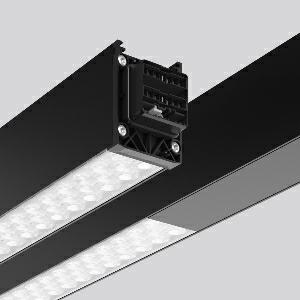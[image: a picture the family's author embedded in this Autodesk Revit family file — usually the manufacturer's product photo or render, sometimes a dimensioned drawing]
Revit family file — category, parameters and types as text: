
# Revit family: linedo_2_3m_90_1000_952390_843_400_704_318a
name_source: partatom
category: Lighting Fixtures
units: mm (PartAtom-declared; Revit-internal decimal feet)

## family parameters
Cut with Voids When Loaded = No
Host = Face
Light Source = No
Part Type = Normal
Room Calculation Point = No
Round Connector Dimension = Use Diameter
Shared = No

## types (1)
- LINEDO_2,3m_90_1000 (1 x LED Modul 840, 5200 lm, 4000)
    Apparent Load = 38 VA
    CIE Flux Codes = 73 96 99 100 100
    Color Rendering = 80
    Color Temperature = 4000
    Default Elevation = 1800 mm
    Description = LINEDO, 38 W, 5200 lm, 840, black, on/off
Continuous line luminaire, L 2291 B 58 H 76
    Height = 76 mm
    Lamp = 1 x LED Modul 840
    Lamp Light Flux = 5200 lm
    Lamp count = 1
    Length = 2291 mm
    Lifetime = 50000 h
    Luminous efficacy = 137 lm/W
    Manufacturer = RZB
    ModVariant = No
    Model = 952390.843.400.704
    Mounting Place = Ceiling
    Mounting Type = Surface mounted, Pendant
    Number of Poles = 1
    OnlyDefault = Yes
    Power Factor = 1
    Product Name = LINEDO_2,3m_90_1000
    Product group = Surface mounted continuous line luminaire system
    ProductGroupID = 310
    Protection Class = Protection class I
    Protection Degree = IP 54
    RLX_Detail_Level = 1
    RLX_Emergency_Light_Flux = 0 lm
    RLX_Emergency_Type = 0
    RLX_Emergency_Type_DB = No
    RlxData = <blob elided: 56541 chars, md5=ba0949ef>
    Socket = socket
    Standby Power = 0 W
    System Light Flux = 5200 lm
    System Power = 38 W
    Type Comments = Product without accessories
    Type Image = 954590.853.476.504.jpg
    URL = http://relux.com
    VarID = ---
    Voltage = 230 V
    Voltage Range = 220-240 V
    Weight = 0.00 kg
    Width = 58 mm

## geometry (parser evidence)
native form markers: Blend x4, Sweep x13
no freeform markers — native parametric forms only
